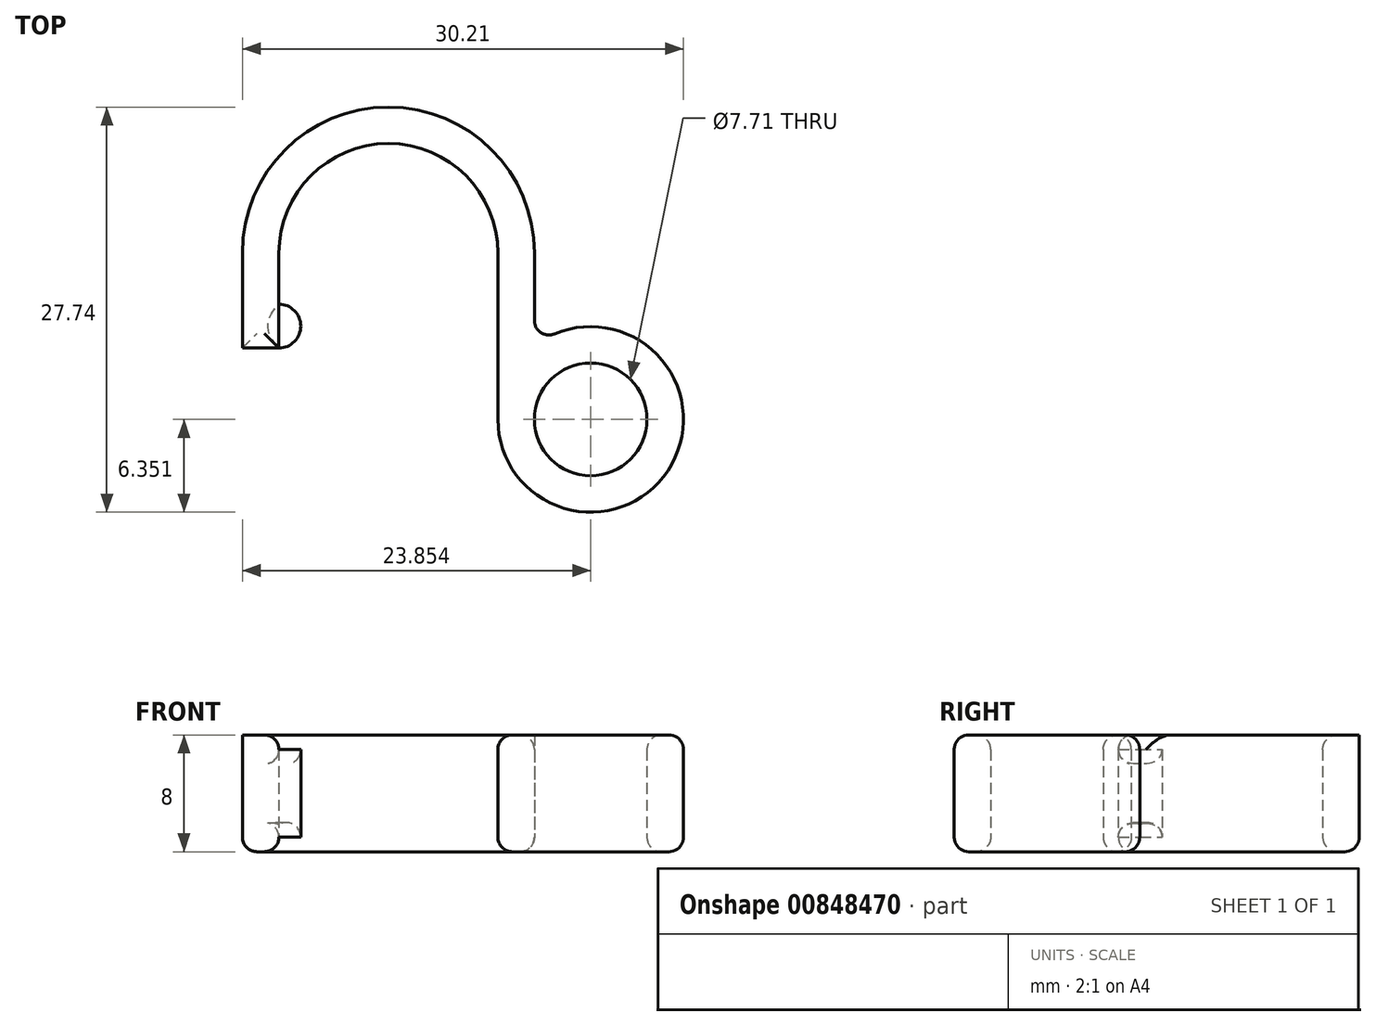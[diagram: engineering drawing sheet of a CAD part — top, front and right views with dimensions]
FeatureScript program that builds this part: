
annotation { "Feature Type Name" : "Feature", "Feature Type Description" : "" }
export const myFeature = defineFeature(function(context is Context, id is Id, definition is map)
    precondition{}
    {
        {
            var Q0;
            Q0=qCreatedBy(makeId("Top.planeOp"),FACE);
            var sketch = newSketch(context, id + "F0", { "sketchPlane" : qUnion([Q0])});
            skArc(sketch, "E0", {"start": v(7.5, 0) * mm, "mid": v(0, 7.5) * mm, "end": v(-7.5, 0) * mm});
            skArc(sketch, "E1", {"start": v(10, 0) * mm, "mid": v(0, 10) * mm, "end": v(-10, 0) * mm});
            skLineSegment(sketch, "E2.left", {"start": v(-10, 0) * mm, "end": v(-10, -6.5) * mm});
            skLineSegment(sketch, "E2.right", {"start": v(-7.5, 0) * mm, "end": v(-7.5, -6.5) * mm});
            skLineSegment(sketch, "E3.left", {"start": v(-7.5, -3.5) * mm, "end": v(-7.5, -6.5) * mm});
            skLineSegment(sketch, "E4", {"start": v(-10, -6.5) * mm, "end": v(-7.5, -6.5) * mm});
            skArc(sketch, "E5", {"start": v(-7.5, -6.5) * mm, "mid": v(-6, -5) * mm, "end": v(-7.5, -3.5) * mm});
            skPoint(sketch, "E5.third.point", {"position": v(-6, -5) * mm});
            skPoint(sketch, "E6.orphan", {"position": v(-6, -3.5) * mm});
            skPoint(sketch, "E7.orphan", {"position": v(-6, -6.5) * mm});
            skLineSegment(sketch, "E8.left", {"start": v(7.5, 0) * mm, "end": v(7.5, -11.39) * mm});
            skLineSegment(sketch, "E8.right", {"start": v(10, 0) * mm, "end": v(10, -6.34) * mm});
            skArc(sketch, "E9", {"start": v(7.5, -11.39) * mm, "mid": v(19.55, -14.2) * mm, "end": v(10, -6.34) * mm});
            skPoint(sketch, "E9.second.point", {"position": v(20.2, -11.39) * mm});
            skPoint(sketch, "E9.third.point", {"position": v(13.67, -17.74) * mm});
            skPoint(sketch, "E10.trimOffspring.end.orphan", {"position": v(24.8, -11.39) * mm});
            skCircle(sketch, "E11", {"center": v(13.85, -11.39) * mm, "radius": 3.85 * mm});
            skPoint(sketch, "E8.top.end.orphan", {"position": v(10, -11.39) * mm});
            skSolve(sketch);
        }
        {
            var Q0;
            {var subQ1=sQuery(id+"F0.wireOp",EDGE,"E0");Q0=makeQuery(id+"F0.imprint","IMPRINT",FACE,{"disambiguationData":[TD([[makeQuery(id+"F0.imprint","IMPRINT",EDGE,{"derivedFrom":subQ1}),-1.0]])]});}
            var Q1;
            {var subQ0=sQuery(id+"F0.wireOp",EDGE,"E5");Q1=makeQuery(id+"F0.imprint","IMPRINT",FACE,{"disambiguationData":[TD([[makeQuery(id+"F0.imprint","IMPRINT",EDGE,{"derivedFrom":subQ0}),1.0]])]});}
            extrude(context, id + "F1", {"entities" : qUnion([Q0, Q1]), "depth" : 8 * mm, "offsetDistance" : 25 * mm});
        }
        {
            var Q0;
            Q0=makeQuery(id+"F1.opExtrude","CAP_FACE",FACE,{"disambiguationData":[OSD([sQuery(id+"F0.wireOp",EDGE,"E0"),sQuery(id+"F0.wireOp",EDGE,"E1"),sQuery(id+"F0.wireOp",EDGE,"E2.left"),sQuery(id+"F0.wireOp",EDGE,"E2.right"),sQuery(id+"F0.wireOp",EDGE,"E4"),sQuery(id+"F0.wireOp",EDGE,"E5"),sQuery(id+"F0.wireOp",EDGE,"E8.left"),sQuery(id+"F0.wireOp",EDGE,"E8.right"),sQuery(id+"F0.wireOp",EDGE,"E9"),sQuery(id+"F0.wireOp",EDGE,"E11")])],"isStart":true});
            var Q1;
            Q1=makeQuery(id+"F1.opExtrude","SWEPT_FACE",FACE,{"disambiguationData":[OSD([sQuery(id+"F0.wireOp",EDGE,"E9")])]});
            var Q2;
            Q2=makeQuery(id+"F1.opExtrude","CAP_EDGE",EDGE,{"disambiguationData":[OSD([sQuery(id+"F0.wireOp",EDGE,"E5")])],"isStart":false});
            var Q3;
            Q3=makeQuery(id+"F1.opExtrude","CAP_EDGE",EDGE,{"disambiguationData":[OSD([sQuery(id+"F0.wireOp",EDGE,"E4")])],"isStart":false});
            var Q4;
            Q4=makeQuery(id+"F1.opExtrude","CAP_EDGE",EDGE,{"disambiguationData":[OSD([sQuery(id+"F0.wireOp",EDGE,"E11")])],"isStart":false});
            fillet(context, id + "F2", {"entities" : qUnion([Q0, Q1, Q2, Q3, Q4]), "radius" : 1 * mm, "tangentPropagation" : true, "allowEdgeOverflow" : false});
        }
    });
